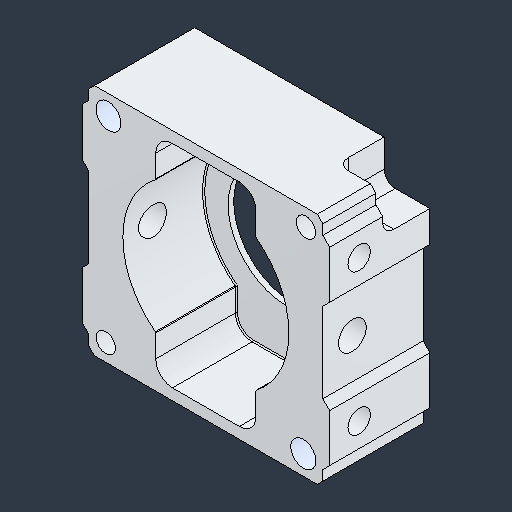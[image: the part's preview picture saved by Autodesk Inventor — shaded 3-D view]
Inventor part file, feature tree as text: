
AUTODESK INVENTOR PART (.ipt)
format: ipt  version: 2024.3 (Build 283343000, 343)  size: 226,816 bytes
history: native  units: in
note: dims shown in document units (in); Inventor stores cm internally (conversion verified against a paired STEP export)
features: chamfer x1
ambient origin geometry x8: Origin, YZ Plane, XZ Plane, XY Plane, X Axis, Y Axis, Z Axis, Center Point
bodies: Solid1 (feature_tree)
feature tree (1):
  chamfer  "Chamfer4"  [1 undecoded]
note: 1 required parameter value undecoded (feature->parameter linkage not recoverable at this tier; creation-order binding heuristic only, values carry confidence <= 0.55)
